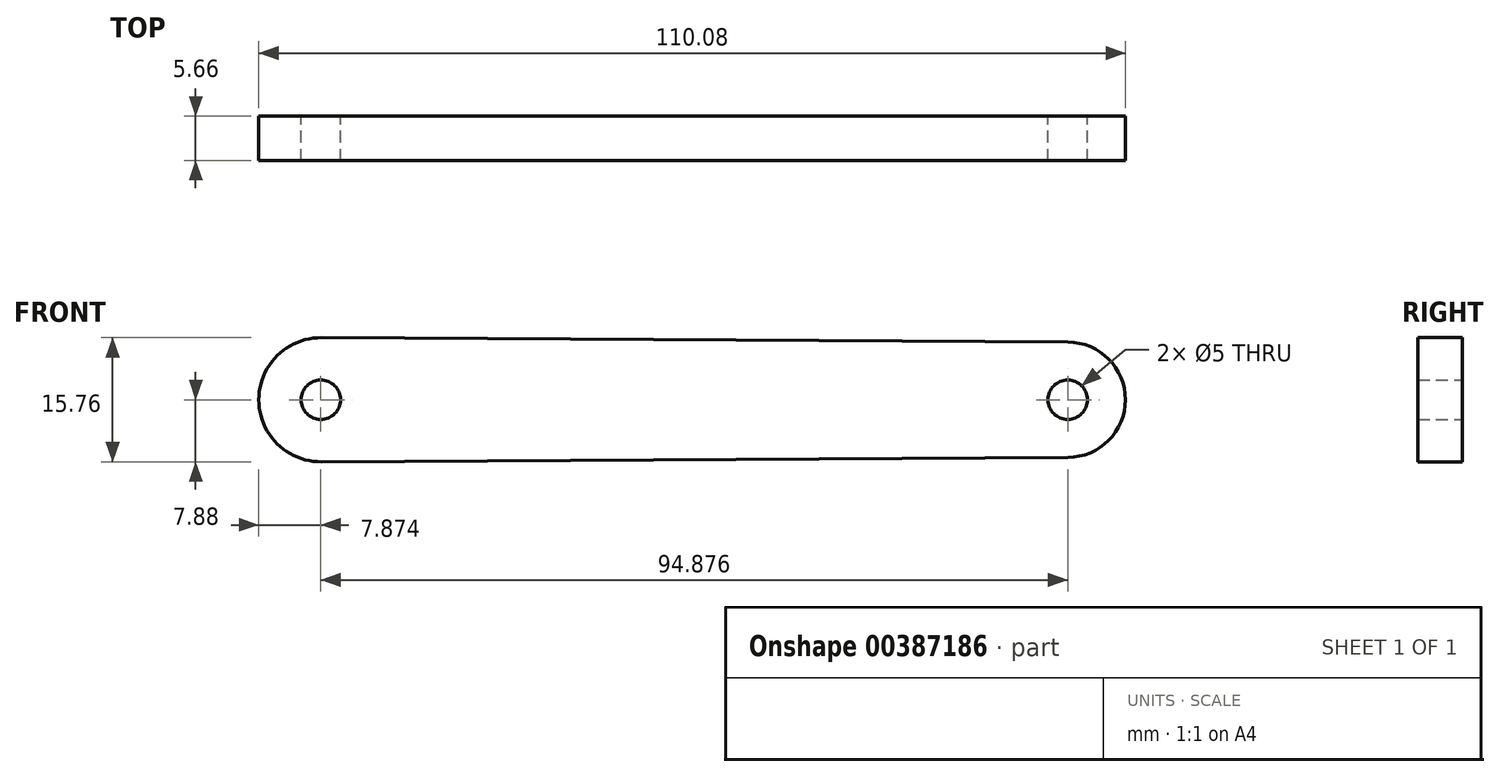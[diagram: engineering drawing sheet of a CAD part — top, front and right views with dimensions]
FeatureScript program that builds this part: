
annotation { "Feature Type Name" : "Feature", "Feature Type Description" : "" }
export const myFeature = defineFeature(function(context is Context, id is Id, definition is map)
    precondition{}
    {
        {
            var Q0;
            Q0=qCreatedBy(makeId("Front.planeOp"),FACE);
            var sketch = newSketch(context, id + "F0", { "sketchPlane" : qUnion([Q0])});
            skCircle(sketch, "E0", {"center": v(-56.02, 0) * mm, "radius": 2.5 * mm});
            skCircle(sketch, "E1", {"center": v(38.86, 0) * mm, "radius": 2.5 * mm});
            skCircle(sketch, "E2", {"center": v(-56.02, 0) * mm, "radius": 7.88 * mm});
            skCircle(sketch, "E3", {"center": v(38.86, 0) * mm, "radius": 7.33 * mm});
            skLineSegment(sketch, "E4", {"start": v(-56.02, 7.88) * mm, "end": v(38.9, 7.33) * mm});
            skLineSegment(sketch, "E5", {"start": v(-56.02, -7.88) * mm, "end": v(38.9, -7.33) * mm});
            skSolve(sketch);
        }
        {
            var Q0;
            Q0 = qSketchRegion(id + "F0", true);
            extrude(context, id + "F1", {"entities" : qUnion([Q0]), "depth" : 5.66 * mm});
        }
    });
